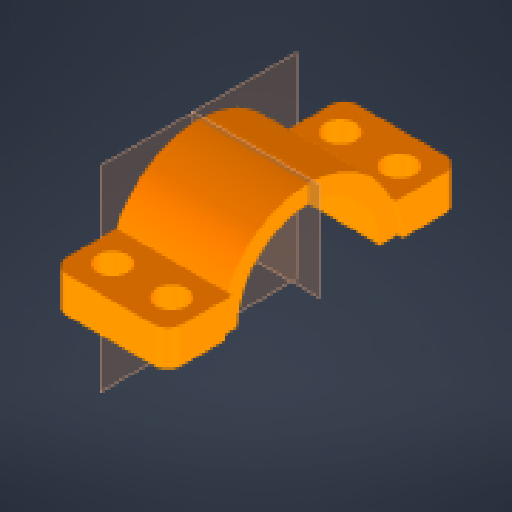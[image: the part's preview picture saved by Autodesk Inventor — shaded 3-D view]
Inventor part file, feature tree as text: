
AUTODESK INVENTOR PART (.ipt)
format: ipt  version: 2024 (Build 280153000, 153)  size: 184,832 bytes
history: native  units: mm
features: other x12, reference x7, sketch x3, extrude x3, fillet x1, mirror x1
ambient origin geometry x8: Origin, YZ Plane, XZ Plane, XY Plane, X Axis, Y Axis, Z Axis, Center Point
bodies: Body1 (feature_tree)
feature tree (27):
  other  "Твердое тело1"
  sketch  "Эскиз1"
  other  "РабПлоскость1"
  extrude  "Выдавливание1"  Depth=10.0mm TaperAngle=0.0deg
  fillet  "Сопряжение1"  Radius=2.0mm
  extrude  "Выдавливание2"  Depth=10.0mm TaperAngle=0.0deg
  other  "РабПлоскость2"
  sketch  "Эскиз3"
  other  "РабПлоскость3"
  extrude  "Выдавливание3"  Depth=10.0mm TaperAngle=0.0deg
  other  "РабПлоскость6"
  mirror  "Зеркальное отражение1"
  reference  "Ссылка1"
  reference  "Ссылка3"
  reference  "Ссылка4"
  sketch  "Эскиз2"
  reference  "Ссылка5"
  reference  "Ссылка6"
  reference  "Ссылка7"
  reference  "Ссылка8"
  parser-record x1  (decoder bookkeeping rows leaked as tree rows — omitted from the tree; the rows remain in map.json)
  other  "default_motor_asembly.iam"
  other  "lower_arm:1"
  other  "bushing_assembly:1"
  other  "bushing:1"
  other  "DIN 125-1 A A 4,3:4"
  other  "DIN 125-1 A A 4,3:3"
note: 1 file-system path scrubbed to <path> (originals preserved in map.json)
